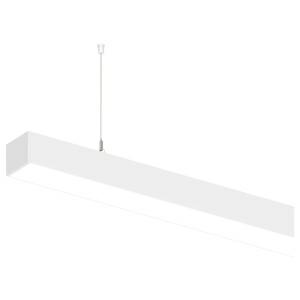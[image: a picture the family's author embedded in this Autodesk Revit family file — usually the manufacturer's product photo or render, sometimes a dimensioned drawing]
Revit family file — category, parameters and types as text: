
# Revit family: idaho_100_dir_ind_2290x102_hl_led_76w_8170lm_3000k_cri80_430-5230_cd74
name_source: partatom
category: Lighting Fixtures
units: mm (PartAtom-declared; Revit-internal decimal feet)

## family parameters
Cut with Voids When Loaded = No
Host = Face
Light Source = No
Part Type = Normal
Room Calculation Point = No
Round Connector Dimension = Use Diameter
Shared = No

## types (1)
- 430-5230-D01 (15 x LED, 710 lm, 5.1 W, 3000K)
    Apparent Load = 77 VA
    CIE Flux Codes = 48 79 96 62 67
    Color Rendering = 1B/80…89
    Color Temperature = 3000K
    Default Elevation = 1800 mm
    Description = The pendant luminaire IDAHO 100 from the familiy IDAHO consists of aluminum. The ballast is integrated and allows for an operation with 220-240V (50/60Hz). IDAHO 100 (# 430-5230) ist not dimmable (on/off). The luminaire with direct and indirect illumination corresponds to protection class SK1 at IP20.
    Height = 90 mm
    Lamp = 15 x LED
    Lamp Light Flux = 710 lm
    Lamp Power = 5.1 W
    Lamp count = 15
    Length = 2290 mm
    Luminous efficacy = 94 lm/W
    Manufacturer = Prolicht
    ModVariant = No
    Model = 430-5230
    Mounting Place = Ceiling
    Mounting Type = Pendant
    Number of Poles = 1
    OnlyDefault = Yes
    Power Factor = 1
    Product Name = IDAHO 100 DIR/IND 2290x102 HL LED 76W 8170lm 3000K CRI80
    Product group = Suspended profile lights
    ProductGroupID = 943
    Protection Class = Protection class
    Protection Degree = Degree of protection
    RLX_Detail_Level = 1
    RlxData = <blob elided: 66797 chars, md5=8c39026a>
    Socket = socket
    Standby Power = 0 W
    System Light Flux = 7157 lm
    System Power = 77 W
    Type Image = 430-5230.jpg
    URL = http://relux.com
    VarID = 430-5230-d01
    Voltage = 0 V
    Weight = 0.00 kg
    Width = 102 mm

## geometry (parser evidence)
native form markers: Blend x4, Sweep x15
no freeform markers — native parametric forms only
